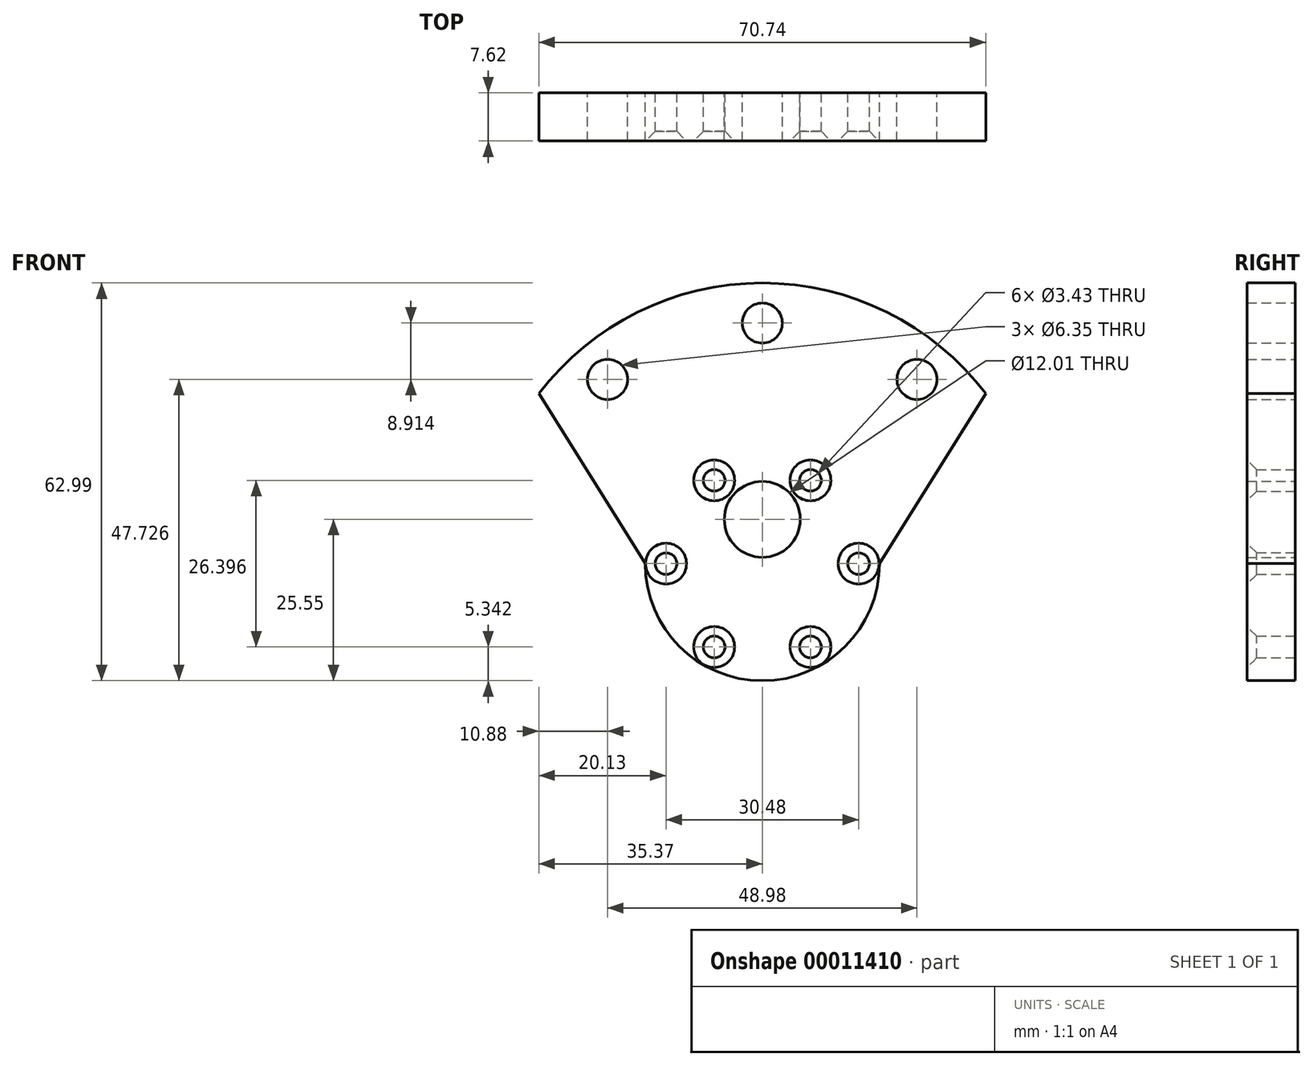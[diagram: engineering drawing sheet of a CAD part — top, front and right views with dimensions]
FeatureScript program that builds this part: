
annotation { "Feature Type Name" : "Feature", "Feature Type Description" : "" }
export const myFeature = defineFeature(function(context is Context, id is Id, definition is map)
    precondition{}
    {
        {
            var Q0;
            Q0=qCreatedBy(makeId("Front.planeOp"),FACE);
            var sketch = newSketch(context, id + "F0", { "sketchPlane" : qUnion([Q0])});
            skArc(sketch, "E0", {"start": v(35.37, 26.93) * mm, "mid": v(0, 44.45) * mm, "end": v(-35.37, 26.93) * mm});
            skCircle(sketch, "E1", {"center": v(0, 0) * mm, "radius": 38.1 * mm, "construction": true});
            skCircle(sketch, "E2", {"center": v(0, 38.1) * mm, "radius": 3.18 * mm});
            skCircle(sketch, "E3.1.0", {"center": v(-24.5, 29.19) * mm, "radius": 3.18 * mm});
            skCircle(sketch, "E4", {"center": v(0, 0) * mm, "radius": 15.24 * mm, "construction": true});
            skArc(sketch, "E5", {"start": v(-18.54, 0) * mm, "mid": v(0, -18.54) * mm, "end": v(18.54, 0) * mm});
            skCircle(sketch, "E6.1.8.0", {"center": v(24.5, 29.19) * mm, "radius": 3.18 * mm});
            skLineSegment(sketch, "E7", {"start": v(-18.54, 0) * mm, "end": v(-35.37, 26.93) * mm});
            skLineSegment(sketch, "E8", {"start": v(18.54, 0) * mm, "end": v(35.37, 26.93) * mm});
            skCircle(sketch, "E9", {"center": v(-15.24, 0) * mm, "radius": 1.71 * mm});
            skCircle(sketch, "E10.1.0", {"center": v(-7.62, -13.2) * mm, "radius": 1.71 * mm});
            skCircle(sketch, "E10.2.0", {"center": v(7.62, -13.2) * mm, "radius": 1.71 * mm});
            skCircle(sketch, "E10.3.0", {"center": v(15.24, 0) * mm, "radius": 1.71 * mm});
            skCircle(sketch, "E10.4.0", {"center": v(7.62, 13.2) * mm, "radius": 1.71 * mm});
            skCircle(sketch, "E10.5.0", {"center": v(-7.62, 13.2) * mm, "radius": 1.71 * mm});
            skCircle(sketch, "E11", {"center": v(0, 7.01) * mm, "radius": 6 * mm});
            skSolve(sketch);
        }
        {
            var Q0;
            Q0 = qSketchRegion(id + "F0", true);
            extrude(context, id + "F1", {"entities" : qUnion([Q0]), "depth" : 7.62 * mm});
        }
        {
            var Q0;
            Q0=makeQuery(id+"F1.opExtrude","CAP_EDGE",EDGE,{"disambiguationData":[OSD([sQuery(id+"F0.wireOp",EDGE,"E9")])],"isStart":false});
            var Q1;
            Q1=makeQuery(id+"F1.opExtrude","CAP_EDGE",EDGE,{"disambiguationData":[OSD([sQuery(id+"F0.wireOp",EDGE,"E10.5.0")])],"isStart":false});
            var Q2;
            Q2=makeQuery(id+"F1.opExtrude","CAP_EDGE",EDGE,{"disambiguationData":[OSD([sQuery(id+"F0.wireOp",EDGE,"E10.4.0")])],"isStart":false});
            var Q3;
            Q3=makeQuery(id+"F1.opExtrude","CAP_EDGE",EDGE,{"disambiguationData":[OSD([sQuery(id+"F0.wireOp",EDGE,"E10.3.0")])],"isStart":false});
            var Q4;
            Q4=makeQuery(id+"F1.opExtrude","CAP_EDGE",EDGE,{"disambiguationData":[OSD([sQuery(id+"F0.wireOp",EDGE,"E10.2.0")])],"isStart":false});
            var Q5;
            Q5=makeQuery(id+"F1.opExtrude","CAP_EDGE",EDGE,{"disambiguationData":[OSD([sQuery(id+"F0.wireOp",EDGE,"E10.1.0")])],"isStart":false});
            chamfer(context, id + "F2", {"entities" : qUnion([Q0, Q1, Q2, Q3, Q4, Q5]), "width" : 1.52 * mm, "tangentPropagation" : true});
        }
    });
